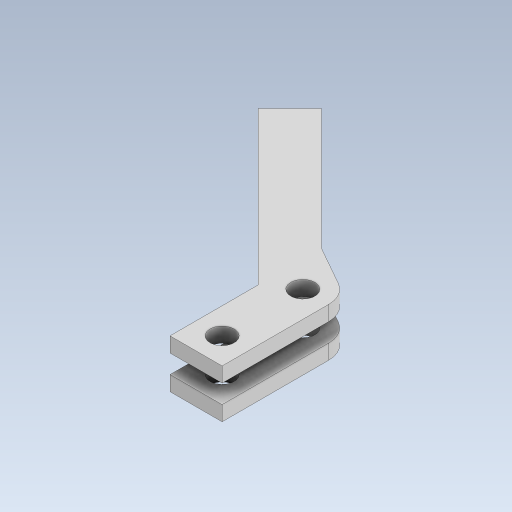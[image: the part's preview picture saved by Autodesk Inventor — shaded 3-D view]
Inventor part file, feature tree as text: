
AUTODESK INVENTOR PART (.ipt)
format: ipt  version: 2023 (Build 270158000, 158)  size: 332,288 bytes
history: native  units: in
note: dims shown in document units (in); Inventor stores cm internally (conversion verified against a paired STEP export)
features: extrude x2, fillet x1, mirror x1, projected_geometry x1
ambient origin geometry x8: Origin, YZ Plane, XZ Plane, XY Plane, X Axis, Y Axis, Z Axis, Center Point
bodies: Solid1 (feature_tree)
feature tree (5):
  extrude  "Extrusion1"  Depth=0.2559in
  fillet  "Fillet1"  Radius=0.8543in
  extrude  "Extrusion4"  Depth=0.2756in
  mirror  "Mirror3"
  projected_geometry  "Projected Loop1"
